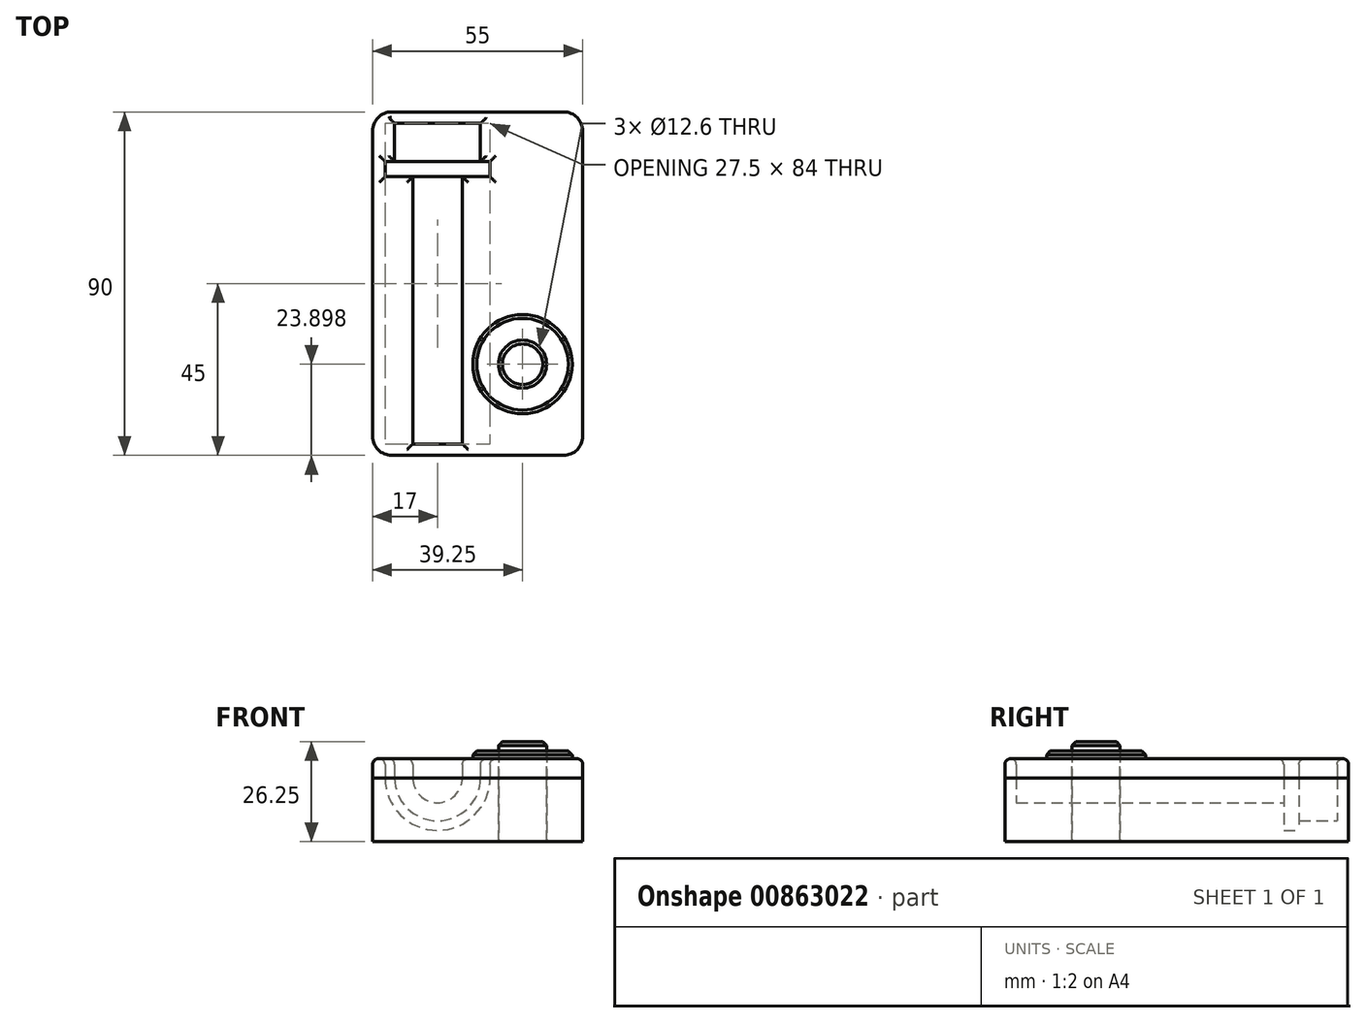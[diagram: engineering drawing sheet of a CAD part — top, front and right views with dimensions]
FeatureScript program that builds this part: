
annotation { "Feature Type Name" : "Feature", "Feature Type Description" : "" }
export const myFeature = defineFeature(function(context is Context, id is Id, definition is map)
    precondition{}
    {
        {
            var Q0;
            Q0=qCreatedBy(makeId("Top.planeOp"),FACE);
            var sketch = newSketch(context, id + "F0", { "sketchPlane" : qUnion([Q0])});
            skLineSegment(sketch, "E0.bottom", {"start": v(27.5, 45) * mm, "end": v(-27.5, 45) * mm});
            skLineSegment(sketch, "E0.top", {"start": v(27.5, -45) * mm, "end": v(-27.5, -45) * mm});
            skLineSegment(sketch, "E0.left", {"start": v(27.5, 45) * mm, "end": v(27.5, -45) * mm});
            skLineSegment(sketch, "E0.right", {"start": v(-27.5, 45) * mm, "end": v(-27.5, -45) * mm});
            skPoint(sketch, "E0.middle", {"position": v(0, 0) * mm});
            skSolve(sketch);
        }
        {
            var Q0;
            Q0 = qSketchRegion(id + "F0", true);
            extrude(context, id + "F1", {"entities" : qUnion([Q0]), "oppositeDirection" : true, "depth" : 16.75 * mm, "offsetDistance" : 25 * mm});
        }
        {
            var Q0;
            Q0=makeQuery(id+"F1.opExtrude","CAP_FACE",FACE,{"disambiguationData":[OSD([sQuery(id+"F0.wireOp",EDGE,"E0.bottom"),sQuery(id+"F0.wireOp",EDGE,"E0.top"),sQuery(id+"F0.wireOp",EDGE,"E0.left"),sQuery(id+"F0.wireOp",EDGE,"E0.right")])],"isStart":true});
            var sketch = newSketch(context, id + "F2", { "sketchPlane" : qUnion([Q0])});
            skLineSegment(sketch, "E1", {"start": v(-10.5, 42) * mm, "end": v(0.75, 42) * mm});
            skLineSegment(sketch, "E2", {"start": v(0.75, 42) * mm, "end": v(0.75, 32) * mm});
            skLineSegment(sketch, "E3", {"start": v(0.75, 32) * mm, "end": v(3.25, 32) * mm});
            skLineSegment(sketch, "E4", {"start": v(3.25, 32) * mm, "end": v(3.25, 28) * mm});
            skLineSegment(sketch, "E5", {"start": v(3.25, 28) * mm, "end": v(-4, 28) * mm});
            skLineSegment(sketch, "E6", {"start": v(-4, 28) * mm, "end": v(-4, -42) * mm});
            skLineSegment(sketch, "E7", {"start": v(-4, -42) * mm, "end": v(-10.5, -42) * mm});
            skLineSegment(sketch, "E8", {"start": v(-10.5, -42) * mm, "end": v(-10.5, 42) * mm});
            skLineSegment(sketch, "E9", {"start": v(-10.5, 0) * mm, "end": v(-4, 0) * mm, "construction": true});
            skLineSegment(sketch, "E10", {"start": v(-27.5, 0) * mm, "end": v(27.5, 0) * mm, "construction": true});
            skSolve(sketch);
        }
        {
            var Q0;
            Q0=makeQuery(id+"F2.imprint","IMPRINT",FACE,{"disambiguationData":[TD([[makeQuery(id+"F2.imprint","IMPRINT",EDGE,{"derivedFrom":sQuery(id+"F2.wireOp",EDGE,"E1")}),-1.0]])]});
            var Q1;
            Q1=sQuery(id+"F2.wireOp",EDGE,"E8");
            revolve(context, id + "F3", {"operationType" : NewBodyOperationType.REMOVE, "surfaceOperationType" : NewSurfaceOperationType.NEW, "entities" : qUnion([Q0]), "axis" : qUnion([Q1]), "revolveType" : RevolveType.FULL, "oppositeDirection" : true});
        }
        {
            var Q0;
            Q0=makeQuery(id+"F1.opExtrude","CAP_FACE",FACE,{"disambiguationData":[OSD([sQuery(id+"F0.wireOp",EDGE,"E0.bottom"),sQuery(id+"F0.wireOp",EDGE,"E0.top"),sQuery(id+"F0.wireOp",EDGE,"E0.left"),sQuery(id+"F0.wireOp",EDGE,"E0.right")])],"isStart":true});
            var sketch = newSketch(context, id + "F4", { "sketchPlane" : qUnion([Q0])});
            skCircle(sketch, "E11", {"center": v(12.5, -25) * mm, "radius": 13 * mm});
            skSolve(sketch);
        }
        {
            var Q0;
            Q0 = qSketchRegion(id + "F4", true);
            extrude(context, id + "F5", {"entities" : qUnion([Q0]), "depth" : 2 * mm, "offsetDistance" : 25 * mm});
        }
        {
            var Q0;
            Q0=makeQuery(id+"F5.opExtrude","SWEPT_BODY",BODY,{"disambiguationData":[OSD([sQuery(id+"F4.wireOp",EDGE,"E11")])]});
            deleteBodies(context, id + "F6", {"entities" : qUnion([Q0])});
        }
        {
            var Q0;
            Q0=makeQuery(id+"F1.opExtrude","CAP_FACE",FACE,{"disambiguationData":[OSD([sQuery(id+"F0.wireOp",EDGE,"E0.bottom"),sQuery(id+"F0.wireOp",EDGE,"E0.top"),sQuery(id+"F0.wireOp",EDGE,"E0.left"),sQuery(id+"F0.wireOp",EDGE,"E0.right")])],"isStart":true});
            var sketch = newSketch(context, id + "F7", { "sketchPlane" : qUnion([Q0])});
            skLineSegment(sketch, "E12.0.0", {"start": v(-27.5, -45) * mm, "end": v(27.5, -45) * mm});
            skLineSegment(sketch, "E12.0.1", {"start": v(27.5, -45) * mm, "end": v(27.5, 45) * mm});
            skLineSegment(sketch, "E12.0.2", {"start": v(27.5, 45) * mm, "end": v(-27.5, 45) * mm});
            skLineSegment(sketch, "E12.0.3", {"start": v(-27.5, 45) * mm, "end": v(-27.5, -45) * mm});
            skLineSegment(sketch, "E13.0", {"start": v(0.75, 42) * mm, "end": v(-21.75, 42) * mm});
            skLineSegment(sketch, "E14.0", {"start": v(-21.75, 42) * mm, "end": v(-21.75, 32) * mm});
            skLineSegment(sketch, "E15.0", {"start": v(-21.75, 32) * mm, "end": v(-24.25, 32) * mm});
            skLineSegment(sketch, "E16.0", {"start": v(-24.25, 32) * mm, "end": v(-24.25, 28) * mm});
            skLineSegment(sketch, "E17.0", {"start": v(-24.25, 28) * mm, "end": v(-17, 28) * mm});
            skLineSegment(sketch, "E18.0", {"start": v(-17, 28) * mm, "end": v(-17, -42) * mm});
            skLineSegment(sketch, "E19.0", {"start": v(-4, -42) * mm, "end": v(-4, 28) * mm});
            skLineSegment(sketch, "E20.0", {"start": v(-4, 28) * mm, "end": v(3.25, 28) * mm});
            skLineSegment(sketch, "E21.0", {"start": v(3.25, 28) * mm, "end": v(3.25, 32) * mm});
            skLineSegment(sketch, "E22.0", {"start": v(3.25, 32) * mm, "end": v(0.75, 32) * mm});
            skLineSegment(sketch, "E23.0", {"start": v(0.75, 32) * mm, "end": v(0.75, 42) * mm});
            skLineSegment(sketch, "E24.0", {"start": v(-17, -42) * mm, "end": v(-4, -42) * mm});
            skSolve(sketch);
        }
        {
            var Q0;
            Q0 = qSketchRegion(id + "F7", true);
            extrude(context, id + "F8", {"entities" : qUnion([Q0]), "depth" : 5 * mm, "offsetDistance" : 25 * mm});
        }
        {
            var Q0;
            Q0=makeQuery(id+"F8.opExtrude","CAP_FACE",FACE,{"disambiguationData":[OSD([sQuery(id+"F7.wireOp",EDGE,"E12.0.0"),sQuery(id+"F7.wireOp",EDGE,"E12.0.1"),sQuery(id+"F7.wireOp",EDGE,"E12.0.2"),sQuery(id+"F7.wireOp",EDGE,"E12.0.3"),sQuery(id+"F7.wireOp",EDGE,"E13.0"),sQuery(id+"F7.wireOp",EDGE,"E14.0"),sQuery(id+"F7.wireOp",EDGE,"E15.0"),sQuery(id+"F7.wireOp",EDGE,"E16.0"),sQuery(id+"F7.wireOp",EDGE,"E17.0"),sQuery(id+"F7.wireOp",EDGE,"E18.0"),sQuery(id+"F7.wireOp",EDGE,"E19.0"),sQuery(id+"F7.wireOp",EDGE,"E20.0"),sQuery(id+"F7.wireOp",EDGE,"E21.0"),sQuery(id+"F7.wireOp",EDGE,"E22.0"),sQuery(id+"F7.wireOp",EDGE,"E23.0"),sQuery(id+"F7.wireOp",EDGE,"E24.0")])],"isStart":false});
            var sketch = newSketch(context, id + "F9", { "sketchPlane" : qUnion([Q0])});
            skCircle(sketch, "E25", {"center": v(11.75, -21.1) * mm, "radius": 13 * mm});
            skLineSegment(sketch, "E26", {"start": v(-4, -21.1) * mm, "end": v(27.5, -21.1) * mm, "construction": true});
            skSolve(sketch);
        }
        {
            var Q0;
            Q0 = qSketchRegion(id + "F9", true);
            extrude(context, id + "F10", {"entities" : qUnion([Q0]), "depth" : 2 * mm, "offsetDistance" : 25 * mm});
        }
        {
            var Q0;
            Q0=makeQuery(id+"F10.opExtrude","CAP_FACE",FACE,{"disambiguationData":[OSD([sQuery(id+"F9.wireOp",EDGE,"E25")])],"isStart":false});
            var sketch = newSketch(context, id + "F11", { "sketchPlane" : qUnion([Q0])});
            skPoint(sketch, "E27", {"position": v(11.75, -21.1) * mm});
            skCircle(sketch, "E28", {"center": v(11.75, -21.1) * mm, "radius": 6.3 * mm});
            skSolve(sketch);
        }
        {
            var Q0;
            Q0 = qSketchRegion(id + "F11", true);
            extrude(context, id + "F12", {"entities" : qUnion([Q0]), "operationType" : NewBodyOperationType.REMOVE, "endBound" : BoundingType.THROUGH_ALL, "oppositeDirection" : true, "depth" : 25 * mm, "offsetDistance" : 25 * mm});
        }
        {
            var Q0;
            Q0=makeQuery(id+"F1.opExtrude","SWEPT_EDGE",EDGE,{"disambiguationData":[OSD([sQuery(id+"F0.wireOp",EDGE,"E0.top"),sQuery(id+"F0.wireOp",EDGE,"E0.right")])]});
            var Q1;
            Q1=makeQuery(id+"F8.opExtrude","SWEPT_EDGE",EDGE,{"disambiguationData":[OSD([sQuery(id+"F7.wireOp",EDGE,"E12.0.0"),sQuery(id+"F7.wireOp",EDGE,"E12.0.3")])]});
            var Q2;
            Q2=makeQuery(id+"F8.opExtrude","SWEPT_EDGE",EDGE,{"disambiguationData":[OSD([sQuery(id+"F7.wireOp",EDGE,"E12.0.0"),sQuery(id+"F7.wireOp",EDGE,"E12.0.1")])]});
            var Q3;
            Q3=makeQuery(id+"F1.opExtrude","SWEPT_EDGE",EDGE,{"disambiguationData":[OSD([sQuery(id+"F0.wireOp",EDGE,"E0.top"),sQuery(id+"F0.wireOp",EDGE,"E0.left")])]});
            var Q4;
            Q4=makeQuery(id+"F8.opExtrude","SWEPT_EDGE",EDGE,{"disambiguationData":[OSD([sQuery(id+"F7.wireOp",EDGE,"E12.0.1"),sQuery(id+"F7.wireOp",EDGE,"E12.0.2")])]});
            var Q5;
            Q5=makeQuery(id+"F1.opExtrude","SWEPT_EDGE",EDGE,{"disambiguationData":[OSD([sQuery(id+"F0.wireOp",EDGE,"E0.bottom"),sQuery(id+"F0.wireOp",EDGE,"E0.left")])]});
            var Q6;
            Q6=makeQuery(id+"F8.opExtrude","SWEPT_EDGE",EDGE,{"disambiguationData":[OSD([sQuery(id+"F7.wireOp",EDGE,"E12.0.2"),sQuery(id+"F7.wireOp",EDGE,"E12.0.3")])]});
            var Q7;
            Q7=makeQuery(id+"F1.opExtrude","SWEPT_EDGE",EDGE,{"disambiguationData":[OSD([sQuery(id+"F0.wireOp",EDGE,"E0.bottom"),sQuery(id+"F0.wireOp",EDGE,"E0.right")])]});
            fillet(context, id + "F13", {"entities" : qUnion([Q0, Q1, Q2, Q3, Q4, Q5, Q6, Q7]), "radius" : 5 * mm, "tangentPropagation" : true, "allowEdgeOverflow" : false});
        }
        {
            var Q0;
            Q0=makeQuery(id+"F10.opExtrude","CAP_EDGE",EDGE,{"disambiguationData":[OSD([sQuery(id+"F9.wireOp",EDGE,"E25")])],"isStart":false});
            chamfer(context, id + "F14", {"entities" : qUnion([Q0]), "width" : 1 * mm, "tangentPropagation" : true});
        }
        {
            var Q0;
            Q0=makeQuery(id+"F8.opExtrude","CAP_EDGE",EDGE,{"disambiguationData":[OSD([sQuery(id+"F7.wireOp",EDGE,"E13.0")])],"isStart":false});
            var Q1;
            Q1=makeQuery(id+"F8.opExtrude","CAP_EDGE",EDGE,{"disambiguationData":[OSD([sQuery(id+"F7.wireOp",EDGE,"E14.0")])],"isStart":false});
            var Q2;
            Q2=makeQuery(id+"F8.opExtrude","CAP_EDGE",EDGE,{"disambiguationData":[OSD([sQuery(id+"F7.wireOp",EDGE,"E15.0")])],"isStart":false});
            var Q3;
            Q3=makeQuery(id+"F8.opExtrude","CAP_EDGE",EDGE,{"disambiguationData":[OSD([sQuery(id+"F7.wireOp",EDGE,"E16.0")])],"isStart":false});
            var Q4;
            Q4=makeQuery(id+"F8.opExtrude","CAP_EDGE",EDGE,{"disambiguationData":[OSD([sQuery(id+"F7.wireOp",EDGE,"E17.0")])],"isStart":false});
            var Q5;
            Q5=makeQuery(id+"F8.opExtrude","CAP_EDGE",EDGE,{"disambiguationData":[OSD([sQuery(id+"F7.wireOp",EDGE,"E18.0")])],"isStart":false});
            var Q6;
            Q6=makeQuery(id+"F8.opExtrude","CAP_EDGE",EDGE,{"disambiguationData":[OSD([sQuery(id+"F7.wireOp",EDGE,"E24.0")])],"isStart":false});
            var Q7;
            Q7=makeQuery(id+"F8.opExtrude","CAP_EDGE",EDGE,{"disambiguationData":[OSD([sQuery(id+"F7.wireOp",EDGE,"E19.0")])],"isStart":false});
            var Q8;
            Q8=makeQuery(id+"F8.opExtrude","CAP_EDGE",EDGE,{"disambiguationData":[OSD([sQuery(id+"F7.wireOp",EDGE,"E20.0")])],"isStart":false});
            var Q9;
            Q9=makeQuery(id+"F8.opExtrude","CAP_EDGE",EDGE,{"disambiguationData":[OSD([sQuery(id+"F7.wireOp",EDGE,"E21.0")])],"isStart":false});
            var Q10;
            Q10=makeQuery(id+"F8.opExtrude","CAP_EDGE",EDGE,{"disambiguationData":[OSD([sQuery(id+"F7.wireOp",EDGE,"E22.0")])],"isStart":false});
            var Q11;
            Q11=makeQuery(id+"F8.opExtrude","CAP_EDGE",EDGE,{"disambiguationData":[OSD([sQuery(id+"F7.wireOp",EDGE,"E23.0")])],"isStart":false});
            var Q12;
            Q12=makeQuery(id+"F8.opExtrude","CAP_EDGE",EDGE,{"disambiguationData":[OSD([sQuery(id+"F7.wireOp",EDGE,"E12.0.1")])],"isStart":false});
            fillet(context, id + "F15", {"entities" : qUnion([Q0, Q1, Q2, Q3, Q4, Q5, Q6, Q7, Q8, Q9, Q10, Q11, Q12]), "radius" : 1.5 * mm, "tangentPropagation" : true, "allowEdgeOverflow" : false});
        }
        {
            var Q0;
            Q0=makeQuery(id+"F1.opExtrude","CAP_FACE",FACE,{"disambiguationData":[OSD([sQuery(id+"F0.wireOp",EDGE,"E0.bottom"),sQuery(id+"F0.wireOp",EDGE,"E0.top"),sQuery(id+"F0.wireOp",EDGE,"E0.left"),sQuery(id+"F0.wireOp",EDGE,"E0.right")])],"isStart":false});
            var sketch = newSketch(context, id + "F16", { "sketchPlane" : qUnion([Q0])});
            skCircle(sketch, "E29.0", {"center": v(11.75, 21.1) * mm, "radius": 6.3 * mm});
            skSolve(sketch);
        }
        {
            var Q0;
            Q0 = qSketchRegion(id + "F16", true);
            extrude(context, id + "F17", {"entities" : qUnion([Q0]), "oppositeDirection" : true, "depth" : 26.25 * mm, "offsetDistance" : 25 * mm});
        }
        {
            var Q0;
            Q0=makeQuery(id+"F17.opExtrude","CAP_EDGE",EDGE,{"disambiguationData":[OSD([sQuery(id+"F16.wireOp",EDGE,"E29.0")])],"isStart":false});
            chamfer(context, id + "F18", {"entities" : qUnion([Q0]), "width" : 1 * mm, "tangentPropagation" : true});
        }
    });
